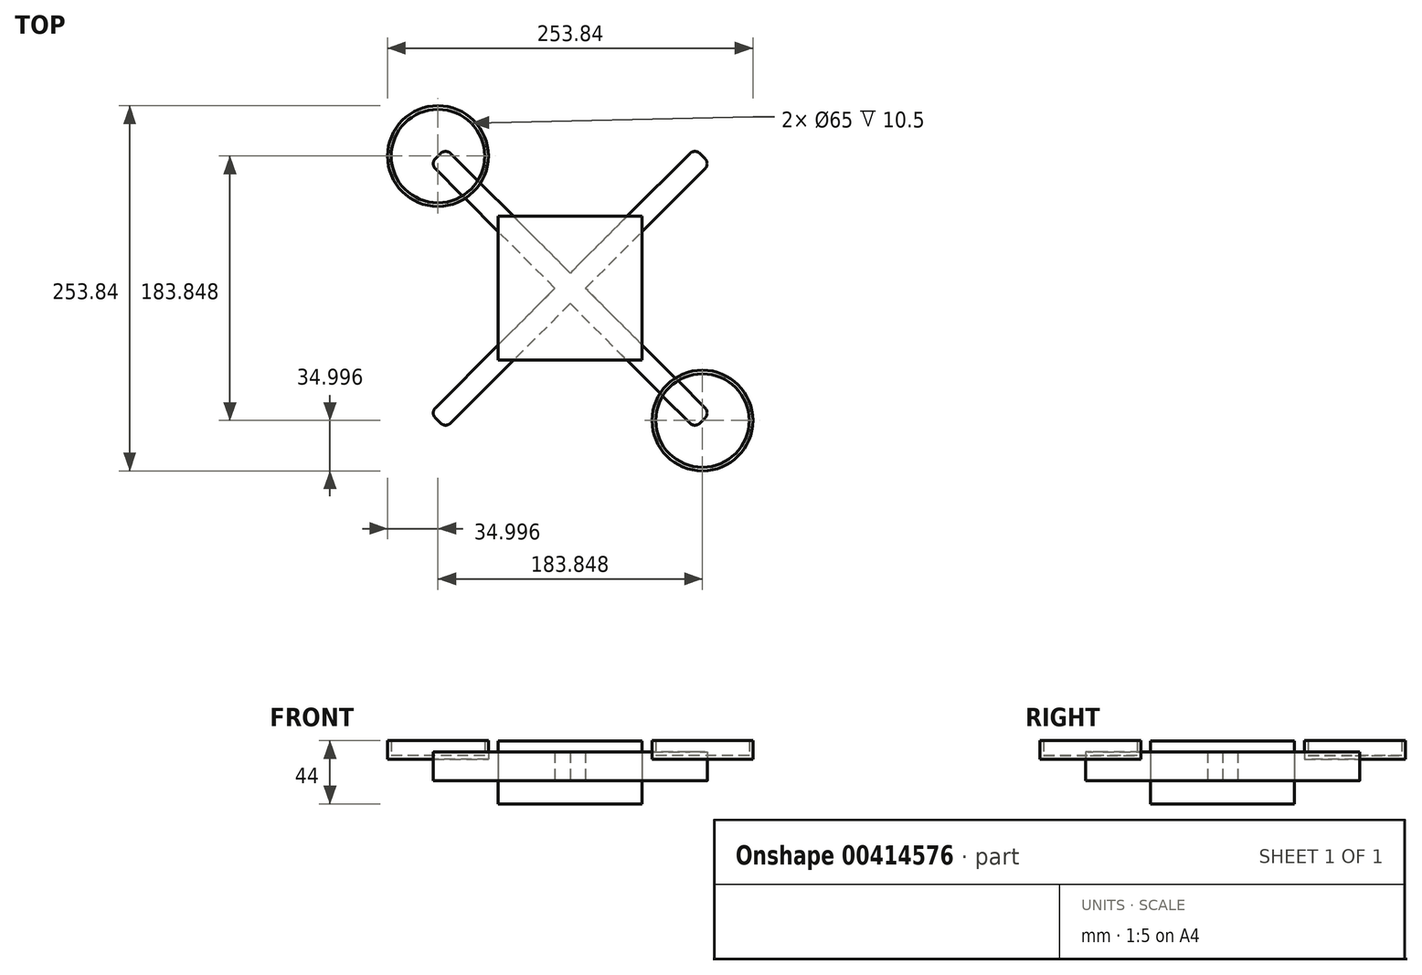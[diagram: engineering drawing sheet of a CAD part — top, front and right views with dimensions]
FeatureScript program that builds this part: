
annotation { "Feature Type Name" : "Feature", "Feature Type Description" : "" }
export const myFeature = defineFeature(function(context is Context, id is Id, definition is map)
    precondition{}
    {
        {
            var Q0;
            Q0=qCreatedBy(makeId("Top.planeOp"),FACE);
            var sketch = newSketch(context, id + "F0", { "sketchPlane" : qUnion([Q0])});
            skLineSegment(sketch, "E0.bottom", {"start": v(-50, 50) * mm, "end": v(50, 50) * mm});
            skLineSegment(sketch, "E0.top", {"start": v(-50, -50) * mm, "end": v(50, -50) * mm});
            skLineSegment(sketch, "E0.left", {"start": v(-50, 50) * mm, "end": v(-50, -50) * mm});
            skLineSegment(sketch, "E0.right", {"start": v(50, 50) * mm, "end": v(50, -50) * mm});
            skSolve(sketch);
        }
        {
            var Q0;
            Q0=qCreatedBy(makeId("Top.planeOp"),FACE);
            var sketch = newSketch(context, id + "F1", { "sketchPlane" : qUnion([Q0])});
            skCircle(sketch, "E1", {"center": v(91.92, -91.92) * mm, "radius": 35 * mm});
            skCircle(sketch, "E2", {"center": v(0, 0) * mm, "radius": 130 * mm, "construction": true});
            skLineSegment(sketch, "E3", {"start": v(0, 0) * mm, "end": v(91.92, -91.92) * mm, "construction": true});
            skCircle(sketch, "E4.MirrorC", {"center": v(-91.92, -91.92) * mm, "radius": 35 * mm});
            skCircle(sketch, "E5.MirrorC", {"center": v(-91.92, 91.92) * mm, "radius": 35 * mm});
            skCircle(sketch, "E6.MirrorC", {"center": v(91.92, 91.92) * mm, "radius": 35 * mm});
            skSolve(sketch);
        }
        {
            var Q0;
            Q0=qCreatedBy(makeId("Top.planeOp"),FACE);
            var sketch = newSketch(context, id + "F2", { "sketchPlane" : qUnion([Q0])});
            skLineSegment(sketch, "E7", {"start": v(-97.23, 86.62) * mm, "end": v(86.62, -97.23) * mm});
            skLineSegment(sketch, "E8", {"start": v(86.62, -97.23) * mm, "end": v(97.23, -86.62) * mm});
            skLineSegment(sketch, "E9", {"start": v(97.23, -86.62) * mm, "end": v(-86.62, 97.23) * mm});
            skLineSegment(sketch, "E10", {"start": v(-86.62, 97.23) * mm, "end": v(-97.23, 86.62) * mm});
            skLineSegment(sketch, "E11", {"start": v(-91.92, 91.92) * mm, "end": v(91.92, -91.92) * mm, "construction": true});
            skLineSegment(sketch, "E12.1.0", {"start": v(-86.62, -97.23) * mm, "end": v(97.23, 86.62) * mm});
            skLineSegment(sketch, "E12.1.1", {"start": v(86.62, 97.23) * mm, "end": v(-97.23, -86.62) * mm});
            skLineSegment(sketch, "E12.1.2", {"start": v(91.92, 91.92) * mm, "end": v(-91.92, -91.92) * mm, "construction": true});
            skLineSegment(sketch, "E12.1.3", {"start": v(-97.23, -86.62) * mm, "end": v(-86.62, -97.23) * mm});
            skLineSegment(sketch, "E12.1.4", {"start": v(97.23, 86.62) * mm, "end": v(86.62, 97.23) * mm});
            skPoint(sketch, "E12.center", {"position": v(0, 0) * mm});
            skSolve(sketch);
        }
        {
            var Q0;
            Q0=qCreatedBy(makeId("Top.planeOp"),FACE);
            cPlane(context, id + "F3", {"entities" : qUnion([Q0]), "cplaneType" : CPlaneType.OFFSET, "offset" : 31 * mm, "width" : 150 * mm, "height" : 150 * mm});
        }
        {
            var Q0;
            Q0=qCreatedBy(id+"F3.planeOp",FACE);
            var sketch = newSketch(context, id + "F4", { "sketchPlane" : qUnion([Q0])});
            skCircle(sketch, "E13.0", {"center": v(91.92, 91.92) * mm, "radius": 35 * mm});
            skCircle(sketch, "E14.0", {"center": v(91.92, -91.92) * mm, "radius": 35 * mm});
            skCircle(sketch, "E15.0", {"center": v(-91.92, 91.92) * mm, "radius": 35 * mm});
            skCircle(sketch, "E16.0", {"center": v(-91.92, -91.92) * mm, "radius": 35 * mm});
            skSolve(sketch);
        }
        {
            var Q0;
            Q0=makeQuery(id+"F4.imprint","IMPRINT",FACE,{"disambiguationData":[TD([[makeQuery(id+"F4.imprint","IMPRINT",EDGE,{"derivedFrom":sQuery(id+"F4.wireOp",EDGE,"E13.0")}),-1.0]])]});
            var Q1;
            Q1=makeQuery(id+"F4.imprint","IMPRINT",FACE,{"disambiguationData":[TD([[makeQuery(id+"F4.imprint","IMPRINT",EDGE,{"derivedFrom":sQuery(id+"F4.wireOp",EDGE,"E15.0")}),1.0]])]});
            var Q2;
            Q2=makeQuery(id+"F4.imprint","IMPRINT",FACE,{"disambiguationData":[TD([[makeQuery(id+"F4.imprint","IMPRINT",EDGE,{"derivedFrom":sQuery(id+"F4.wireOp",EDGE,"E16.0")}),-1.0]])]});
            var Q3;
            Q3=makeQuery(id+"F4.imprint","IMPRINT",FACE,{"disambiguationData":[TD([[makeQuery(id+"F4.imprint","IMPRINT",EDGE,{"derivedFrom":sQuery(id+"F4.wireOp",EDGE,"E14.0")}),1.0]])]});
            extrude(context, id + "F5", {"entities" : qUnion([Q0, Q1, Q2, Q3]), "depth" : 13 * mm});
        }
        {
            var Q0;
            Q0=makeQuery(id+"F0.imprint","IMPRINT",FACE,{"disambiguationData":[TD([[makeQuery(id+"F0.imprint","IMPRINT",EDGE,{"derivedFrom":sQuery(id+"F0.wireOp",EDGE,"E0.bottom")}),-1.0]])]});
            extrude(context, id + "F6", {"entities" : qUnion([Q0]), "depth" : 43.8 * mm});
        }
        {
            var Q0;
            Q0=qCreatedBy(id+"F3.planeOp",FACE);
            var sketch = newSketch(context, id + "F7", { "sketchPlane" : qUnion([Q0])});
            skLineSegment(sketch, "E17.0.0", {"start": v(97.23, 86.62) * mm, "end": v(86.62, 97.23) * mm});
            skLineSegment(sketch, "E17.0.1", {"start": v(86.62, 97.23) * mm, "end": v(0, 10.6) * mm});
            skLineSegment(sketch, "E17.0.3", {"start": v(10.6, 0) * mm, "end": v(97.23, 86.62) * mm});
            skLineSegment(sketch, "E18.0.1", {"start": v(0, -10.6) * mm, "end": v(86.62, -97.23) * mm});
            skLineSegment(sketch, "E18.0.2", {"start": v(86.62, -97.23) * mm, "end": v(97.23, -86.62) * mm});
            skLineSegment(sketch, "E18.0.3", {"start": v(97.23, -86.62) * mm, "end": v(10.6, 0) * mm});
            skLineSegment(sketch, "E19.MirrorCS", {"start": v(-86.62, -97.23) * mm, "end": v(-97.23, -86.62) * mm});
            skLineSegment(sketch, "E20.MirrorCS", {"start": v(-97.23, 86.62) * mm, "end": v(-86.62, 97.23) * mm});
            skLineSegment(sketch, "E21.MirrorCS", {"start": v(-86.62, 97.23) * mm, "end": v(0, 10.6) * mm});
            skLineSegment(sketch, "E22.MirrorCS", {"start": v(-97.23, -86.62) * mm, "end": v(-10.6, 0) * mm});
            skLineSegment(sketch, "E23.MirrorCS", {"start": v(0, -10.6) * mm, "end": v(-86.62, -97.23) * mm});
            skLineSegment(sketch, "E24.MirrorCS", {"start": v(-10.6, 0) * mm, "end": v(-97.23, 86.62) * mm});
            skSolve(sketch);
        }
        {
            var Q0;
            Q0=makeQuery(id+"F7.imprint","IMPRINT",FACE,{"disambiguationData":[TD([[makeQuery(id+"F7.imprint","IMPRINT",EDGE,{"derivedFrom":sQuery(id+"F7.wireOp",EDGE,"E17.0.0")}),1.0]])]});
            var Q1;
            Q1=makeQuery(id+"F5.opExtrude","CAP_FACE",FACE,{"disambiguationData":[OSD([sQuery(id+"F4.wireOp",EDGE,"E13.0")])],"isStart":false});
            extrude(context, id + "F8", {"entities" : qUnion([Q0]), "endBoundEntityFace" : qUnion([Q1]), "depth" : 5 * mm, "hasSecondDirection" : true, "secondDirectionOppositeDirection" : true, "secondDirectionDepth" : 15 * mm});
        }
        {
            var Q0;
            Q0=makeQuery(id+"F8.opExtrude","SWEPT_FACE",FACE,{"disambiguationData":[OSD([sQuery(id+"F7.wireOp",EDGE,"E17.0.3")])]});
            var sketch = newSketch(context, id + "F9", { "sketchPlane" : qUnion([Q0])});
            skLineSegment(sketch, "E25.0", {"start": v(130, 31) * mm, "end": v(130, 16) * mm});
            skLineSegment(sketch, "E26.0", {"start": v(70.71, 16) * mm, "end": v(130, 16) * mm});
            skLineSegment(sketch, "E27", {"start": v(130, 31) * mm, "end": v(70.71, 16) * mm});
            skPoint(sketch, "E28.orphan", {"position": v(130, 36) * mm});
            skPoint(sketch, "E29.orphan", {"position": v(165, 31) * mm});
            skPoint(sketch, "E30.0.end.orphan", {"position": v(95, 31) * mm});
            skPoint(sketch, "E31.orphan", {"position": v(70.71, 43.8) * mm});
            skPoint(sketch, "E32.0.end.orphan", {"position": v(70.71, 0) * mm});
            skPoint(sketch, "E33.orphan", {"position": v(7.5, 16) * mm});
            skSolve(sketch);
        }
        {
            var Q0;
            Q0=makeQuery(id+"F5.opExtrude","CAP_FACE",FACE,{"disambiguationData":[OSD([sQuery(id+"F4.wireOp",EDGE,"E14.0")])],"isStart":false});
            var Q1;
            Q1=makeQuery(id+"F5.opExtrude","CAP_FACE",FACE,{"disambiguationData":[OSD([sQuery(id+"F4.wireOp",EDGE,"E16.0")])],"isStart":false});
            var Q2;
            Q2=makeQuery(id+"F5.opExtrude","CAP_FACE",FACE,{"disambiguationData":[OSD([sQuery(id+"F4.wireOp",EDGE,"E13.0")])],"isStart":false});
            var Q3;
            Q3=makeQuery(id+"F5.opExtrude","CAP_FACE",FACE,{"disambiguationData":[OSD([sQuery(id+"F4.wireOp",EDGE,"E15.0")])],"isStart":false});
            shell(context, id + "F10", {"entities" : qUnion([Q0, Q1, Q2, Q3]), "thickness" : 2.5 * mm});
        }
        {
            var Q0;
            Q0=makeQuery(id+"F8.opExtrude","SWEPT_EDGE",EDGE,{"disambiguationData":[OSD([sQuery(id+"F7.wireOp",EDGE,"E19.MirrorCS"),sQuery(id+"F7.wireOp",EDGE,"E22.MirrorCS")])]});
            var Q1;
            Q1=makeQuery(id+"F8.opExtrude","SWEPT_EDGE",EDGE,{"disambiguationData":[OSD([sQuery(id+"F7.wireOp",EDGE,"E19.MirrorCS"),sQuery(id+"F7.wireOp",EDGE,"E23.MirrorCS")])]});
            var Q2;
            Q2=makeQuery(id+"F8.opExtrude","SWEPT_EDGE",EDGE,{"disambiguationData":[OSD([sQuery(id+"F7.wireOp",EDGE,"E18.0.2"),sQuery(id+"F7.wireOp",EDGE,"E18.0.3")])]});
            var Q3;
            Q3=makeQuery(id+"F8.opExtrude","SWEPT_EDGE",EDGE,{"disambiguationData":[OSD([sQuery(id+"F7.wireOp",EDGE,"E18.0.1"),sQuery(id+"F7.wireOp",EDGE,"E18.0.2")])]});
            var Q4;
            Q4=makeQuery(id+"F8.opExtrude","SWEPT_EDGE",EDGE,{"disambiguationData":[OSD([sQuery(id+"F7.wireOp",EDGE,"E20.MirrorCS"),sQuery(id+"F7.wireOp",EDGE,"E21.MirrorCS")])]});
            var Q5;
            Q5=makeQuery(id+"F8.opExtrude","SWEPT_EDGE",EDGE,{"disambiguationData":[OSD([sQuery(id+"F7.wireOp",EDGE,"E20.MirrorCS"),sQuery(id+"F7.wireOp",EDGE,"E24.MirrorCS")])]});
            var Q6;
            Q6=makeQuery(id+"F8.opExtrude","SWEPT_EDGE",EDGE,{"disambiguationData":[OSD([sQuery(id+"F7.wireOp",EDGE,"E17.0.0"),sQuery(id+"F7.wireOp",EDGE,"E17.0.3")])]});
            var Q7;
            Q7=makeQuery(id+"F8.opExtrude","SWEPT_EDGE",EDGE,{"disambiguationData":[OSD([sQuery(id+"F7.wireOp",EDGE,"E17.0.0"),sQuery(id+"F7.wireOp",EDGE,"E17.0.1")])]});
            fillet(context, id + "F11", {"entities" : qUnion([Q0, Q1, Q2, Q3, Q4, Q5, Q6, Q7]), "radius" : 5 * mm, "tangentPropagation" : true, "allowEdgeOverflow" : false});
        }
    });
